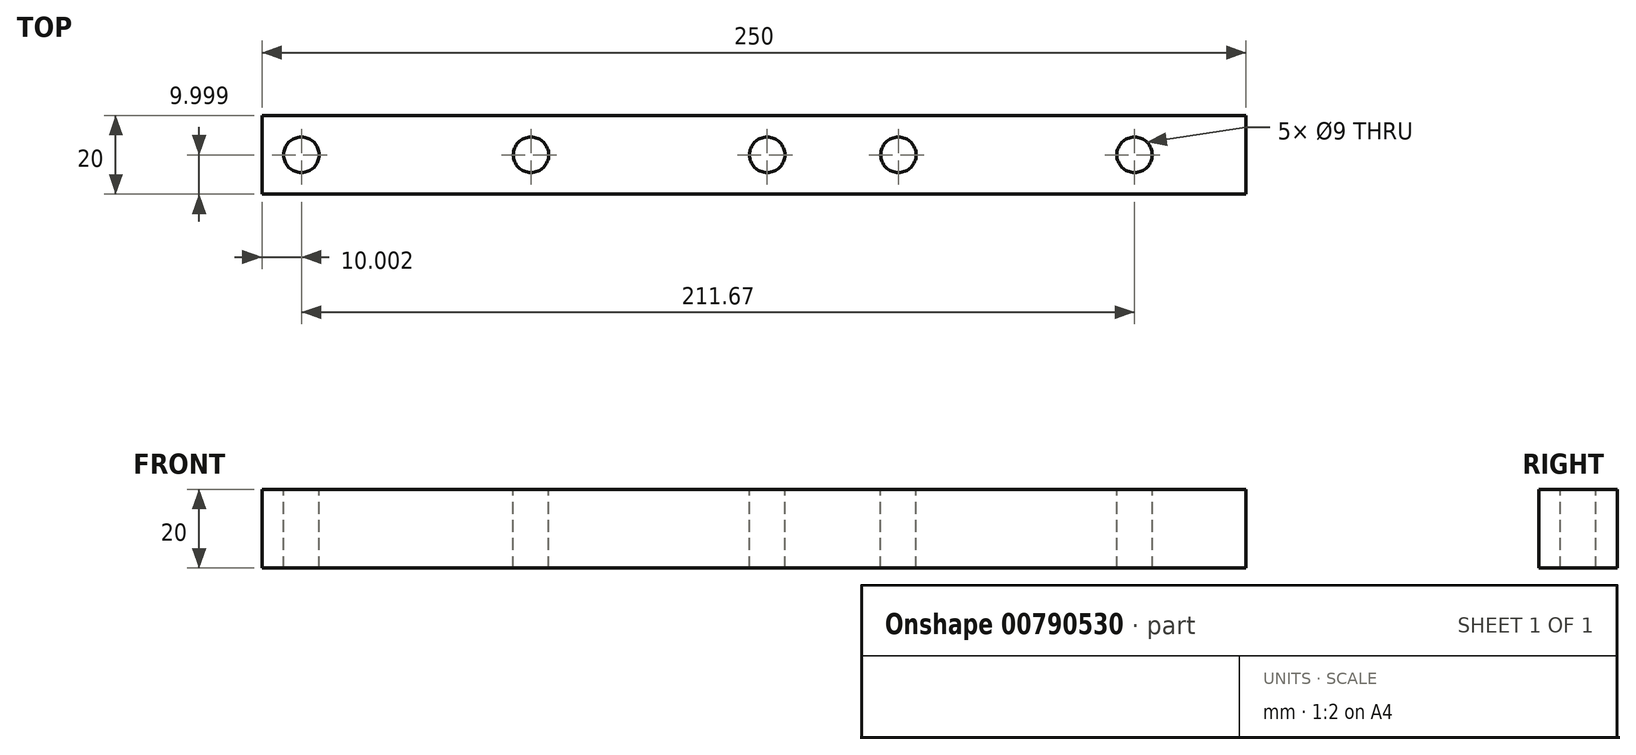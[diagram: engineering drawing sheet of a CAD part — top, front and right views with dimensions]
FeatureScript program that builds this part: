
annotation { "Feature Type Name" : "Feature", "Feature Type Description" : "" }
export const myFeature = defineFeature(function(context is Context, id is Id, definition is map)
    precondition{}
    {
        {
            var Q0;
            Q0=qCreatedBy(makeId("Top.planeOp"),FACE);
            var sketch = newSketch(context, id + "F0", { "sketchPlane" : qUnion([Q0])});
            skLineSegment(sketch, "E0.bottom", {"start": v(-111.86, 36.39) * mm, "end": v(238.14, 36.39) * mm});
            skLineSegment(sketch, "E0.top", {"start": v(-111.86, 16.39) * mm, "end": v(238.14, 16.39) * mm});
            skLineSegment(sketch, "E0.left", {"start": v(-111.86, 36.39) * mm, "end": v(-111.86, 16.39) * mm});
            skLineSegment(sketch, "E0.right", {"start": v(238.14, 36.39) * mm, "end": v(238.14, 16.39) * mm});
            skSolve(sketch);
        }
        {
            var Q0;
            Q0=makeQuery(id+"F0.imprint","IMPRINT",FACE,{"disambiguationData":[TD([[makeQuery(id+"F0.imprint","IMPRINT",EDGE,{"derivedFrom":sQuery(id+"F0.wireOp",EDGE,"E0.bottom")}),-1.0]])]});
            extrude(context, id + "F1", {"entities" : qUnion([Q0]), "depth" : 20 * mm, "offsetDistance" : 25 * mm});
        }
        {
            var Q0;
            Q0=makeQuery(id+"F1.opExtrude","CAP_FACE",FACE,{"disambiguationData":[OSD([sQuery(id+"F0.wireOp",EDGE,"E0.bottom"),sQuery(id+"F0.wireOp",EDGE,"E0.top"),sQuery(id+"F0.wireOp",EDGE,"E0.left"),sQuery(id+"F0.wireOp",EDGE,"E0.right")])],"isStart":false});
            var sketch = newSketch(context, id + "F2", { "sketchPlane" : qUnion([Q0])});
            skLineSegment(sketch, "E1", {"start": v(-111.86, 26.39) * mm, "end": v(-43.53, 26.39) * mm});
            skLineSegment(sketch, "E2", {"start": v(-43.53, 26.39) * mm, "end": v(49.81, 26.39) * mm});
            skPoint(sketch, "E3", {"position": v(-43.53, 26.39) * mm});
            skPoint(sketch, "E4", {"position": v(49.81, 26.39) * mm});
            skSolve(sketch);
        }
        {
            var Q0;
            Q0=sQuery(id+"F2.wireOp",VERTEX,"E3");
            var Q1;
            Q1=sQuery(id+"F2.wireOp",VERTEX,"E4");
            var Q2;
            Q2=makeQuery(id+"F1.opExtrude","SWEPT_BODY",BODY,{"disambiguationData":[OSD([sQuery(id+"F0.wireOp",EDGE,"E0.bottom"),sQuery(id+"F0.wireOp",EDGE,"E0.top"),sQuery(id+"F0.wireOp",EDGE,"E0.left"),sQuery(id+"F0.wireOp",EDGE,"E0.right")])]});
            hole(context, id + "F3", {"style" : HoleStyle.SIMPLE, "endStyle" : HoleEndStyle.THROUGH, "holeDiameter" : 9 * mm, "majorDiameter" : 5 * mm, "isTappedThrough" : true, "tappedDepth" : 12 * mm, "tapClearance" : 3, "locations" : qUnion([Q0, Q1]), "scope" : qUnion([Q2])});
        }
        {
            var Q0;
            Q0=makeQuery(id+"F1.opExtrude","CAP_FACE",FACE,{"disambiguationData":[OSD([sQuery(id+"F0.wireOp",EDGE,"E0.bottom"),sQuery(id+"F0.wireOp",EDGE,"E0.top"),sQuery(id+"F0.wireOp",EDGE,"E0.left"),sQuery(id+"F0.wireOp",EDGE,"E0.right")])],"isStart":false});
            var sketch = newSketch(context, id + "F4", { "sketchPlane" : qUnion([Q0])});
            skLineSegment(sketch, "E5", {"start": v(-111.86, 26.39) * mm, "end": v(-101.86, 26.39) * mm});
            skPoint(sketch, "E6", {"position": v(-101.86, 26.39) * mm});
            skLineSegment(sketch, "E7", {"start": v(238.14, 26.39) * mm, "end": v(228.14, 26.39) * mm});
            skPoint(sketch, "E8", {"position": v(228.14, 26.39) * mm});
            skSolve(sketch);
        }
        {
            var Q0;
            Q0=sQuery(id+"F4.wireOp",VERTEX,"E6");
            var Q1;
            Q1=sQuery(id+"F4.wireOp",VERTEX,"E8");
            var Q2;
            Q2=makeQuery(id+"F1.opExtrude","SWEPT_BODY",BODY,{"disambiguationData":[OSD([sQuery(id+"F0.wireOp",EDGE,"E0.bottom"),sQuery(id+"F0.wireOp",EDGE,"E0.top"),sQuery(id+"F0.wireOp",EDGE,"E0.left"),sQuery(id+"F0.wireOp",EDGE,"E0.right")])]});
            hole(context, id + "F5", {"style" : HoleStyle.SIMPLE, "endStyle" : HoleEndStyle.THROUGH, "holeDiameter" : 9 * mm, "majorDiameter" : 5 * mm, "isTappedThrough" : true, "tappedDepth" : 12 * mm, "tapClearance" : 3, "locations" : qUnion([Q0, Q1]), "scope" : qUnion([Q2])});
        }
        {
            var Q0;
            Q0=makeQuery(id+"F1.opExtrude","CAP_FACE",FACE,{"disambiguationData":[OSD([sQuery(id+"F0.wireOp",EDGE,"E0.bottom"),sQuery(id+"F0.wireOp",EDGE,"E0.top"),sQuery(id+"F0.wireOp",EDGE,"E0.left"),sQuery(id+"F0.wireOp",EDGE,"E0.right")])],"isStart":false});
            var sketch = newSketch(context, id + "F6", { "sketchPlane" : qUnion([Q0])});
            skLineSegment(sketch, "E9", {"start": v(-111.86, 26.39) * mm, "end": v(63.14, 26.39) * mm});
            skLineSegment(sketch, "E10", {"start": v(63.14, 26.39) * mm, "end": v(109.81, 26.39) * mm});
            skLineSegment(sketch, "E11", {"start": v(63.14, 26.39) * mm, "end": v(16.47, 26.39) * mm});
            skPoint(sketch, "E12", {"position": v(16.47, 26.39) * mm});
            skPoint(sketch, "E13", {"position": v(109.81, 26.39) * mm});
            skSolve(sketch);
        }
        {
            var Q0;
            Q0=sQuery(id+"F6.wireOp",VERTEX,"E12");
            var Q1;
            Q1=sQuery(id+"F6.wireOp",VERTEX,"E13");
            var Q2;
            Q2=makeQuery(id+"F1.opExtrude","SWEPT_BODY",BODY,{"disambiguationData":[OSD([sQuery(id+"F0.wireOp",EDGE,"E0.bottom"),sQuery(id+"F0.wireOp",EDGE,"E0.top"),sQuery(id+"F0.wireOp",EDGE,"E0.left"),sQuery(id+"F0.wireOp",EDGE,"E0.right")])]});
            hole(context, id + "F7", {"style" : HoleStyle.SIMPLE, "endStyle" : HoleEndStyle.THROUGH, "holeDiameter" : 9 * mm, "majorDiameter" : 5 * mm, "isTappedThrough" : true, "tappedDepth" : 12 * mm, "tapClearance" : 3, "locations" : qUnion([Q0, Q1]), "scope" : qUnion([Q2])});
        }
        {
            var Q0;
            Q0=makeQuery(id+"F1.opExtrude","CAP_FACE",FACE,{"disambiguationData":[OSD([sQuery(id+"F0.wireOp",EDGE,"E0.bottom"),sQuery(id+"F0.wireOp",EDGE,"E0.top"),sQuery(id+"F0.wireOp",EDGE,"E0.left"),sQuery(id+"F0.wireOp",EDGE,"E0.right")])],"isStart":false});
            var sketch = newSketch(context, id + "F8", { "sketchPlane" : qUnion([Q0])});
            skLineSegment(sketch, "E14", {"start": v(-111.86, 26.39) * mm, "end": v(138.14, 26.39) * mm, "construction": true});
            skLineSegment(sketch, "E15.bottom", {"start": v(138.14, 52.52) * mm, "end": v(251.07, 52.52) * mm});
            skLineSegment(sketch, "E15.top", {"start": v(138.14, 0) * mm, "end": v(251.07, 0) * mm});
            skLineSegment(sketch, "E15.left", {"start": v(138.14, 52.52) * mm, "end": v(138.14, 0) * mm});
            skLineSegment(sketch, "E15.right", {"start": v(251.07, 52.52) * mm, "end": v(251.07, 0) * mm});
            skSolve(sketch);
        }
        {
            var Q0;
            {var subQ0=makeQuery(id+"F1.opExtrude","CAP_EDGE",EDGE,{"disambiguationData":[OSD([sQuery(id+"F0.wireOp",EDGE,"E0.right")])],"isStart":false});Q0=makeQuery(id+"F8.imprint","IMPRINT",FACE,{"disambiguationData":[TD([[makeQuery(id+"F8.imprint","IMPRINT",EDGE,{"derivedFrom":subQ0}),-1.0]])]});}
            extrude(context, id + "F9", {"entities" : qUnion([Q0]), "operationType" : NewBodyOperationType.REMOVE, "oppositeDirection" : true, "depth" : 25 * mm, "offsetDistance" : 25 * mm});
        }
    });
